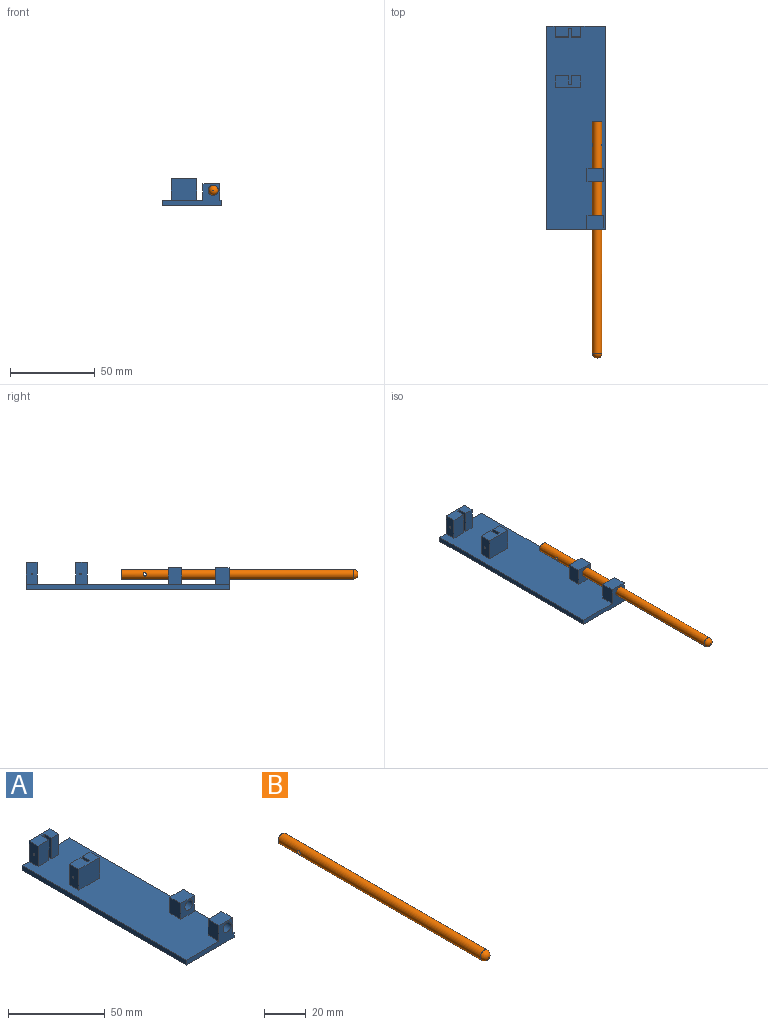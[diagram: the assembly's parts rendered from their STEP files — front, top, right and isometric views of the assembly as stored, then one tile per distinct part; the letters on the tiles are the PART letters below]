
ASSEMBLY  parts=2 mates=1
PART A: 38 faces, bbox 35x120x16 mm
  f0: plane 120x35mm, normal (0,0,1), area 3853.5mm2, adj f1,f3,f4,f5,f6,f7,f8,f9
  f1: plane 120x3mm, normal (-1,0,0), area 360mm2, adj f0,f2,f4,f5
  f2: plane 120x35mm, normal (0,0,-1), area 4200mm2, adj f1,f3,f4,f5
  f3: plane 120x3mm, normal (1,0,0), area 360mm2, adj f0,f2,f4,f5
  f4: plane 35x13mm, normal (0,-1,0), area 176.7mm2, adj f0,f1,f2,f3,f23,f25,f26,f33
  f5: plane 35x16mm, normal (0,1,0), area 302.6mm2, adj f0,f1,f2,f3,f6,f7,f13
  f6: plane 13x6.5mm, normal (1,0,0), area 79.6mm2, adj f0,f5,f12,f13,f35
  f7: plane 13x6.5mm, normal (-1,0,0), area 83.7mm2, adj f0,f5,f8,f13,f37
  f8: plane 13x8mm, normal (0,-1,0), area 104mm2, adj f0,f7,f9,f13
  f9: plane 13x5.2mm, normal (1,0,0), area 66.8mm2, adj f0,f8,f10,f13,f37
  f10: plane 13x1.8mm, normal (0,-1,0), area 23.4mm2, adj f0,f9,f11,f13
  f11: plane 13x5.2mm, normal (-1,0,0), area 62.7mm2, adj f0,f10,f12,f13,f35
  f12: plane 13x5.4mm, normal (0,-1,0), area 70.2mm2, adj f0,f6,f11,f13
  f13: plane 15.2x6.5mm, normal (0,0,1), area 89.4mm2, adj f5,f6,f7,f8,f9,f10,f11,f12
  f14: plane 13x7mm, normal (1,0,0), area 86.1mm2, adj f0,f15,f21,f22,f34
  f15: plane 13x5.4mm, normal (0,1,0), area 70.2mm2, adj f0,f14,f16,f22
  f16: plane 13x5.2mm, normal (-1,0,0), area 62.7mm2, adj f0,f15,f17,f22,f34
  f17: plane 13x1.8mm, normal (0,1,0), area 23.4mm2, adj f0,f16,f18,f22
  f18: plane 13x5.2mm, normal (1,0,0), area 66.8mm2, adj f0,f17,f19,f22,f36
  f19: plane 13x8mm, normal (0,1,0), area 104mm2, adj f0,f18,f20,f22
  f20: plane 13x7mm, normal (-1,0,0), area 90.2mm2, adj f0,f19,f21,f22,f36
  f21: plane 15.2x13mm, normal (0,-1,0), area 197.6mm2, adj f0,f14,f20,f22
  f22: plane 15.2x7mm, normal (0,0,1), area 97mm2, adj f14,f15,f16,f17,f18,f19,f20,f21
  f23: plane 10x8mm, normal (1,0,0), area 80mm2, adj f0,f4,f24,f26
  f24: plane 10x10mm, normal (0,1,0), area 71.7mm2, adj f0,f23,f25,f26,f33
  f25: plane 10x8mm, normal (-1,0,0), area 80mm2, adj f0,f4,f24,f26
  f26: plane 10x8mm, normal (0,0,1), area 80mm2, adj f4,f23,f24,f25
  f27: plane 10x10mm, normal (0,-1,0), area 71.7mm2, adj f0,f28,f30,f31,f32
  f28: plane 10x8mm, normal (1,0,0), area 80mm2, adj f0,f27,f29,f31
  f29: plane 10x10mm, normal (0,1,0), area 71.7mm2, adj f0,f28,f30,f31,f32
  f30: plane 10x8mm, normal (-1,0,0), area 80mm2, adj f0,f27,f29,f31
  f31: plane 10x8mm, normal (0,0,1), area 80mm2, adj f27,f28,f29,f30
  f32: cylinder r=3mm len=8mm, axis (0,1,0), area 150.8mm2, adj f27,f29
  f33: cylinder r=3mm len=8mm, axis (0,1,0), area 150.8mm2, adj f4,f24
  f34: cylinder r=1.25mm len=5.4mm, axis (1,0,0), area 42.4mm2, adj f14,f16
  f35: cylinder r=1.25mm len=5.4mm, axis (1,0,0), area 42.4mm2, adj f6,f11
  f36: cylinder r=0.5mm len=8mm, axis (-1,0,0), area 25.1mm2, adj f18,f20
  f37: cylinder r=0.5mm len=8mm, axis (-1,0,0), area 25.1mm2, adj f7,f9
PART B: 5 faces, bbox 5.6x140x5.6 mm
  f0: cylinder r=2.8mm len=137.3mm, axis (0,1,0), area 2409.1mm2, adj f2,f3,f4
  f1: plane 0.2x0.2mm, normal (0,-1,0), area 0mm2, adj f3
  f2: plane 5.6x5.6mm, normal (0,1,0), area 24.6mm2, adj f0
  f3: torus R=0.1mm, axis (0,-1,0), area 48.5mm2, adj f0,f1
  f4: cylinder r=1mm len=5.6mm, axis (1,0,0), area 34mm2, adj f0
PLACE A at identity fixed
PLACE B rot(axis=(0,-1,0),1.1deg) t=(30,-56.22,6)mm
MATE cylindrical B.f0 <-> A.f32  axis (0,1,0) through (30,-124.87,6)mm
